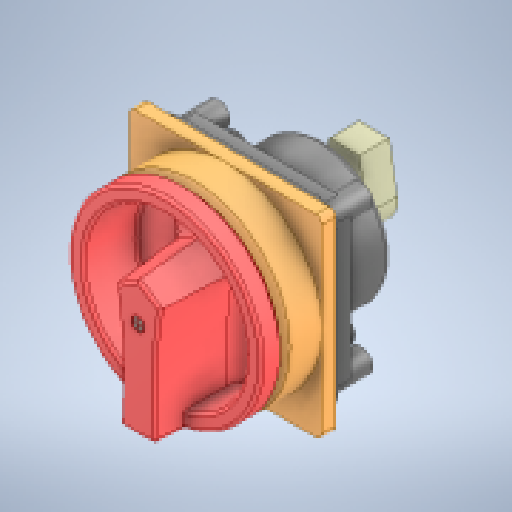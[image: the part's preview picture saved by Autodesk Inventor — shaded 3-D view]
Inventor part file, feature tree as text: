
AUTODESK INVENTOR PART (.ipt)
format: ipt  version: 2025.2 (Build 292293000, 293)  size: 863,232 bytes
history: native  units: mm
features: other x3, fillet x2, direct_edit x1, chamfer x1
ambient origin geometry x8: Origin, YZ Plane, XZ Plane, XY Plane, X Axis, Y Axis, Z Axis, Center Point
bodies: Solid1 (feature_tree), Solid2 (feature_tree), Solid3 (feature_tree), Solid4 (feature_tree)
feature tree (7):
  other  "Plane1"
  direct_edit  "Direct Edit1"
  fillet  "Fillet3"  Radius=6.0mm
  fillet  "Fillet4"  [1 undecoded]
  chamfer  "Chamfer1"  [1 undecoded]
  other  "Move Face1"
  other  "Scale1"
note: 2 required parameter values undecoded (feature->parameter linkage not recoverable at this tier; creation-order binding heuristic only, values carry confidence <= 0.55)
